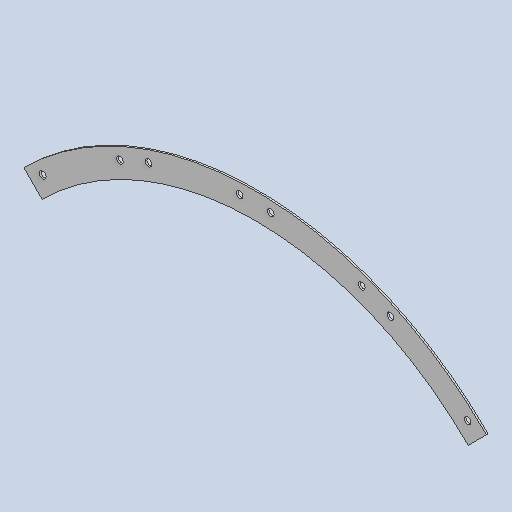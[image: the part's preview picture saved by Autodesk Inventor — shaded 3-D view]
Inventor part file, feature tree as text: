
AUTODESK INVENTOR PART (.ipt)
format: ipt  version: 2025 (Build 290162010, 162A)  size: 184,320 bytes
history: native  units: mm
features: sketch x2, sheet_metal_op x1, hole x1, pattern_circular x1, other x1
ambient origin geometry x8: Origin, YZ Plane, XZ Plane, XY Plane, X Axis, Y Axis, Z Axis, Center Point
bodies: Solid1 (feature_tree)
feature tree (6):
  sheet_metal_op  "Face1"
  hole  "Hole1"  [1 undecoded]
  pattern_circular  "Circular Pattern1"  Count=76  [1 undecoded]
  sketch  "Sketch1"  dims[d15=2.0mm d30=90.0deg d31=760.0mm]
  other  "Plate1"
  sketch  "Sketch2"  dims[d32=700.0mm d34=735.0mm d35=0.490874mm d36=2.945243mm d37=8.0mm d38=6.0mm d39=4.0mm d40=2.0mm d41=90.0deg d42=2.0mm d43=20.594885mm d44=0.490874mm d45=2.945243mm d46=20.0mm d47=45.0deg]
note: 2 required parameter values undecoded (feature->parameter linkage not recoverable at this tier; creation-order binding heuristic only, values carry confidence <= 0.55)
